# Revit family: 2CKA002084A0719
name_source: partatom
category: Elektroinstallationen
revit_build: Autodesk Revit 2017 (Build: 20160225_1515(x64)
units: mm (PartAtom-declared; Revit-internal decimal feet)

## family parameters
Basisbauteil = Fläche
Beim Laden mit Abzugskörper schneiden = Nein
Bemaßung runder Anschluss = Durchmesser verwenden
Beschriftungsausrichtung beibehalten = Nein
Gemeinsam genutzt = Nein
Raumberechnungspunkt = Nein
Teiletyp = Normal

## types (1)
- 2CKA002084A0719
    Anschlussart = Steckklemme
    Anzahl der Einheiten = 2
    Aufdruck/Kennzeichnung = ohne Aufdruck
    Ausführung der Oberfläche = matt
    BIM = https://media.live.bim.site
    BIMSITE_PRODUCT_ID = a54ccb84bc86b91b3c5c42ffdf84991ce7d73c8f
    Befestigungsart = Befestigung mit Schraube
    Beschreibung = SCHUKO Steckdose, grau/blaugrün, Aufputz IP 44, ocean (IP 44), SCHUKO Steckdose mit erh. Berührungsschutz 2-fach Für senkrechte Montage. Mit Steckanschluss. Vorverdrahtet. Mit Klappdeckeln. 2 P + E, Nennstrom: 16 A Schutzart Gerät: IP 44
    Datenblatt = https://media.live.bim.site
    Farbe = blaugrün
    GTIN = 4011395114957
    Geeignet für Schutzart (IP) = IP44
    Gerätebreite [mm] = 74
    Gerätehöhe [mm] = 167
    Gerätetiefe [mm] = 55
    Gewicht [kg/m] = 0.234
    HAN = 2CKA002084A0719
    Halogenfrei = Ja
    HeinzeBIM = https://www.heinze.de
    Hersteller = Busch-Jaeger
    Ist System = Nein
    Ist Zubehör = Nein
    Mit Klappdeckel = Ja
    Mit erhöhtem Berührungsschutz = Ja
    Montageart = Aufputz
    Nennspannung [V] [Volt] = 250
    Nennstrom = 16 A
    Oberfläche = unbehandelt
    Produktseite = https://media.live.bim.site
    Sonderstromversorgung = ohne Sonderstromversorgung
    TYPE = 20-02 EBW-53
    Typname = SCHUKO Steckdose, grau/blaugrün, Aufputz IP 44, ocean (IP 44)
    URL = https://www.busch-jaeger.de
    Vorgabe-Ansicht = 1219 mm
    Werkstoff = Kunststoff
    Werkstoffgüte = Thermoplast

## geometry (parser evidence)
native form markers: Sweep x3
no freeform markers — native parametric forms only
